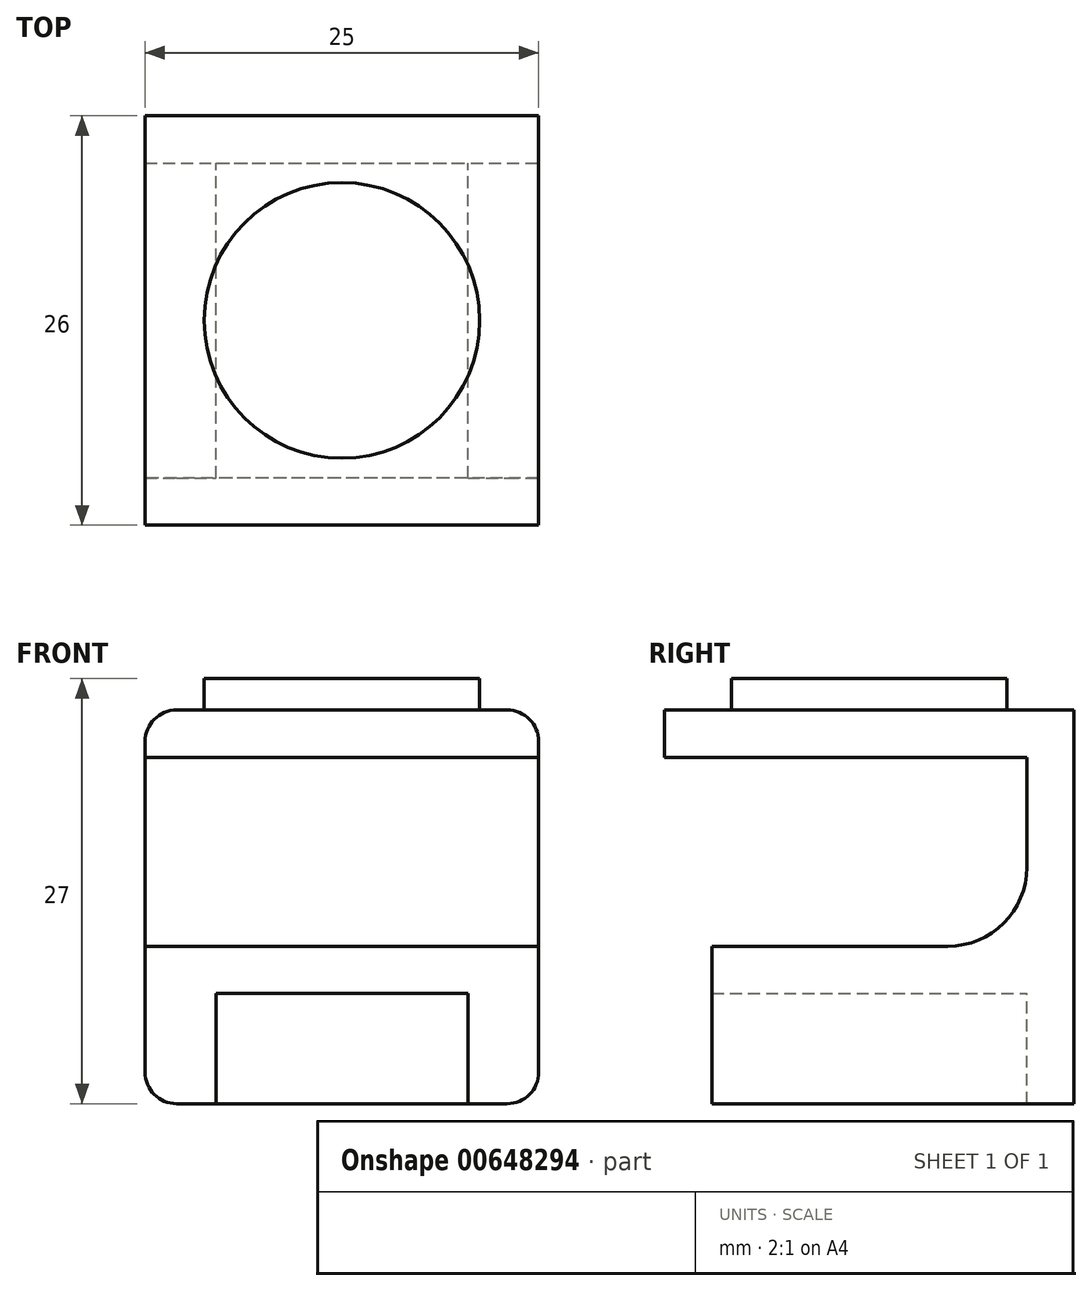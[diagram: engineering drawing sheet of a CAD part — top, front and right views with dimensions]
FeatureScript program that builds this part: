
annotation { "Feature Type Name" : "Feature", "Feature Type Description" : "" }
export const myFeature = defineFeature(function(context is Context, id is Id, definition is map)
    precondition{}
    {
        {
            var Q0;
            Q0=qCreatedBy(makeId("Front.planeOp"),FACE);
            var sketch = newSketch(context, id + "F0", { "sketchPlane" : qUnion([Q0])});
            skLineSegment(sketch, "E0.bottom", {"start": v(0, 0) * mm, "end": v(25, 0) * mm});
            skLineSegment(sketch, "E0.top", {"start": v(0, 25) * mm, "end": v(25, 25) * mm});
            skLineSegment(sketch, "E0.left", {"start": v(0, 0) * mm, "end": v(0, 25) * mm});
            skLineSegment(sketch, "E0.right", {"start": v(25, 0) * mm, "end": v(25, 25) * mm});
            skLineSegment(sketch, "E1", {"start": v(4.5, 0) * mm, "end": v(4.5, 7) * mm});
            skLineSegment(sketch, "E2", {"start": v(4.5, 7) * mm, "end": v(0, 7) * mm});
            skLineSegment(sketch, "E3", {"start": v(20.5, 0) * mm, "end": v(20.5, 7) * mm});
            skLineSegment(sketch, "E4", {"start": v(20.5, 7) * mm, "end": v(25, 7) * mm});
            skLineSegment(sketch, "E5", {"start": v(0, 22) * mm, "end": v(25, 22) * mm});
            skSolve(sketch);
        }
        {
            var Q0;
            {var subQ3=sQuery(id+"F0.wireOp",EDGE,"E1");Q0=makeQuery(id+"F0.imprint","IMPRINT",FACE,{"disambiguationData":[TD([[makeQuery(id+"F0.imprint","IMPRINT",EDGE,{"derivedFrom":subQ3}),-1.0]])]});}
            extrude(context, id + "F1", {"entities" : qUnion([Q0]), "depth" : 3 * mm, "offsetDistance" : 25 * mm});
        }
        {
            var Q0;
            {var subQ3=sQuery(id+"F0.wireOp",EDGE,"E1");Q0=makeQuery(id+"F0.imprint","IMPRINT",FACE,{"disambiguationData":[TD([[makeQuery(id+"F0.imprint","IMPRINT",EDGE,{"derivedFrom":subQ3}),1.0]])]});}
            var Q1;
            {var subQ3=sQuery(id+"F0.wireOp",EDGE,"E3");Q1=makeQuery(id+"F0.imprint","IMPRINT",FACE,{"disambiguationData":[TD([[makeQuery(id+"F0.imprint","IMPRINT",EDGE,{"derivedFrom":subQ3}),-1.0]])]});}
            extrude(context, id + "F2", {"entities" : qUnion([Q0, Q1]), "operationType" : NewBodyOperationType.ADD, "depth" : 23 * mm, "offsetDistance" : 25 * mm});
        }
        {
            var Q0;
            {var subQ0=sQuery(id+"F0.wireOp",EDGE,"E0.top");Q0=makeQuery(id+"F0.imprint","IMPRINT",FACE,{"disambiguationData":[TD([[makeQuery(id+"F0.imprint","IMPRINT",EDGE,{"derivedFrom":subQ0}),-1.0]])]});}
            extrude(context, id + "F3", {"entities" : qUnion([Q0]), "operationType" : NewBodyOperationType.ADD, "depth" : 26 * mm, "offsetDistance" : 25 * mm});
        }
        {
            var Q0;
            Q0=makeQuery(id+"F3.opExtrude","SWEPT_FACE",FACE,{"disambiguationData":[OSD([sQuery(id+"F0.wireOp",EDGE,"E0.top")])]});
            var sketch = newSketch(context, id + "F4", { "sketchPlane" : qUnion([Q0])});
            skPoint(sketch, "E6", {"position": v(12.5, -13) * mm});
            skPoint(sketch, "E6.positionSnap0", {"position": v(12.5, 0) * mm});
            skCircle(sketch, "E7", {"center": v(12.5, -13) * mm, "radius": 8.75 * mm});
            skSolve(sketch);
        }
        {
            var Q0;
            Q0=makeQuery(id+"F4.imprint","IMPRINT",FACE,{"disambiguationData":[TD([[makeQuery(id+"F4.imprint","IMPRINT",EDGE,{"derivedFrom":sQuery(id+"F4.wireOp",EDGE,"E7")}),1.0]])]});
            extrude(context, id + "F5", {"entities" : qUnion([Q0]), "operationType" : NewBodyOperationType.ADD, "depth" : 2 * mm, "offsetDistance" : 25 * mm});
        }
        {
            var Q0;
            Q0=makeQuery(id+"F3.opExtrude","SWEPT_EDGE",EDGE,{"disambiguationData":[OSD([sQuery(id+"F0.wireOp",EDGE,"E0.top"),sQuery(id+"F0.wireOp",EDGE,"E0.left")])]});
            var Q1;
            Q1=makeQuery(id+"F3.opExtrude","SWEPT_EDGE",EDGE,{"disambiguationData":[OSD([sQuery(id+"F0.wireOp",EDGE,"E0.top"),sQuery(id+"F0.wireOp",EDGE,"E0.right")])]});
            var Q2;
            Q2=makeQuery(id+"F2.opExtrude","SWEPT_EDGE",EDGE,{"disambiguationData":[OSD([sQuery(id+"F0.wireOp",EDGE,"E0.bottom"),sQuery(id+"F0.wireOp",EDGE,"E0.left")])]});
            var Q3;
            Q3=makeQuery(id+"F2.opExtrude","SWEPT_EDGE",EDGE,{"disambiguationData":[OSD([sQuery(id+"F0.wireOp",EDGE,"E0.bottom"),sQuery(id+"F0.wireOp",EDGE,"E0.right")])]});
            fillet(context, id + "F6", {"entities" : qUnion([Q0, Q1, Q2, Q3]), "radius" : 2 * mm, "tangentPropagation" : true, "allowEdgeOverflow" : false});
        }
        {
            var Q0;
            Q0=makeQuery(id+"F2.opExtrude","CAP_FACE",FACE,{"disambiguationData":[OSD([sQuery(id+"F0.wireOp",EDGE,"E0.bottom"),sQuery(id+"F0.wireOp",EDGE,"E0.left"),sQuery(id+"F0.wireOp",EDGE,"E1"),sQuery(id+"F0.wireOp",EDGE,"E2")])],"isStart":false});
            var sketch = newSketch(context, id + "F7", { "sketchPlane" : qUnion([Q0])});
            skLineSegment(sketch, "E8", {"start": v(0, 7) * mm, "end": v(25, 7) * mm});
            skLineSegment(sketch, "E9", {"start": v(25, 7) * mm, "end": v(25, 10) * mm});
            skLineSegment(sketch, "E10", {"start": v(25, 10) * mm, "end": v(0, 10) * mm});
            skLineSegment(sketch, "E11", {"start": v(0, 10) * mm, "end": v(0, 7) * mm});
            skSolve(sketch);
        }
        {
            var Q0;
            {var subQ0=sQuery(id+"F7.wireOp",EDGE,"E9");Q0=makeQuery(id+"F7.imprint","IMPRINT",FACE,{"disambiguationData":[TD([[makeQuery(id+"F7.imprint","IMPRINT",EDGE,{"derivedFrom":subQ0}),1.0]])]});}
            var Q1;
            Q1=makeQuery(id+"F1.opExtrude","CAP_FACE",FACE,{"disambiguationData":[OSD([sQuery(id+"F0.wireOp",EDGE,"E0.bottom"),sQuery(id+"F0.wireOp",EDGE,"E0.left"),sQuery(id+"F0.wireOp",EDGE,"E0.right"),sQuery(id+"F0.wireOp",EDGE,"E1"),sQuery(id+"F0.wireOp",EDGE,"E2"),sQuery(id+"F0.wireOp",EDGE,"E3"),sQuery(id+"F0.wireOp",EDGE,"E4"),sQuery(id+"F0.wireOp",EDGE,"E5")])],"isStart":false});
            extrude(context, id + "F8", {"entities" : qUnion([Q0]), "operationType" : NewBodyOperationType.ADD, "endBound" : BoundingType.UP_TO_SURFACE, "oppositeDirection" : true, "depth" : 25 * mm, "endBoundEntityFace" : qUnion([Q1]), "offsetDistance" : 25 * mm});
        }
        {
            var Q0;
            Q0=makeQuery(id+"F8.opExtrude","CAP_EDGE",EDGE,{"disambiguationData":[OSD([sQuery(id+"F7.wireOp",EDGE,"E10")])],"isStart":false});
            var Q1;
            Q1=makeQuery(id+"F1.opExtrude","CAP_EDGE",EDGE,{"disambiguationData":[OSD([sQuery(id+"F0.wireOp",EDGE,"E5")])],"isStart":false});
            fillet(context, id + "F9", {"entities" : qUnion([Q0, Q1]), "radius" : 5 * mm, "tangentPropagation" : true, "allowEdgeOverflow" : false});
        }
    });
